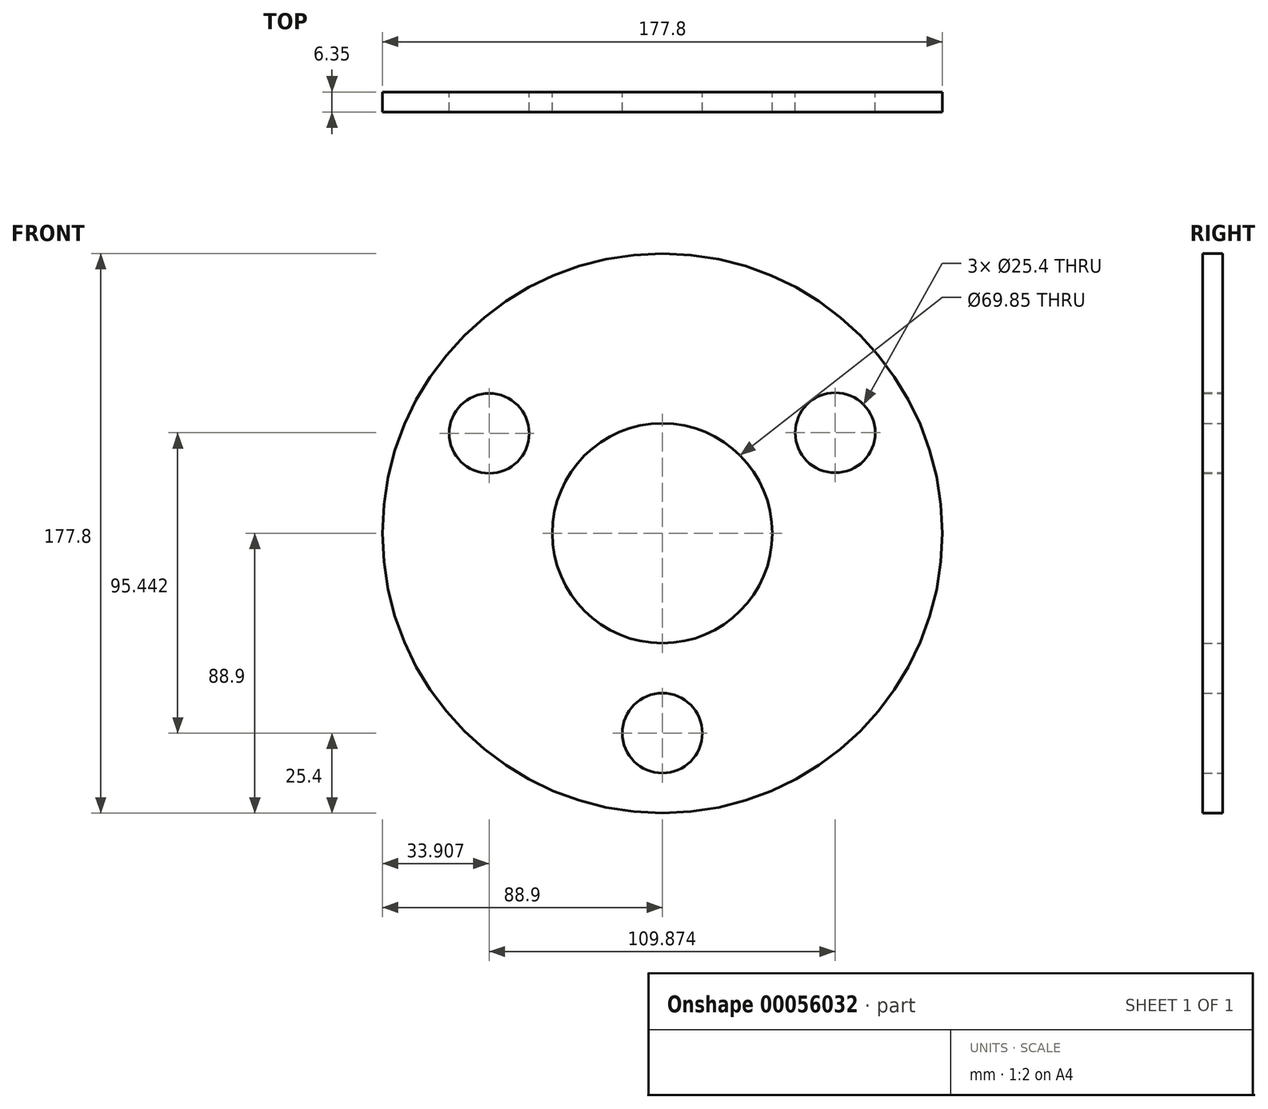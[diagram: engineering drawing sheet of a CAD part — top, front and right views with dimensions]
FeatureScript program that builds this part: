
annotation { "Feature Type Name" : "Feature", "Feature Type Description" : "" }
export const myFeature = defineFeature(function(context is Context, id is Id, definition is map)
    precondition{}
    {
        {
            var Q0;
            Q0=qCreatedBy(makeId("Front.planeOp"),FACE);
            var sketch = newSketch(context, id + "F0", { "sketchPlane" : qUnion([Q0])});
            skCircle(sketch, "E0", {"center": v(0, 0) * mm, "radius": 18.29 * mm});
            skCircle(sketch, "E1", {"center": v(0, 0) * mm, "radius": 34.93 * mm});
            skCircle(sketch, "E2", {"center": v(0, 0) * mm, "radius": 63.5 * mm, "construction": true});
            skCircle(sketch, "E3", {"center": v(0, 0) * mm, "radius": 88.9 * mm});
            skCircle(sketch, "E4", {"center": v(-55, 31.75) * mm, "radius": 12.7 * mm});
            skCircle(sketch, "E5", {"center": v(54.88, 31.94) * mm, "radius": 12.7 * mm});
            skCircle(sketch, "E6", {"center": v(0, -63.5) * mm, "radius": 12.7 * mm});
            skLineSegment(sketch, "E7", {"start": v(0, 0) * mm, "end": v(-88.55, 51.12) * mm});
            skLineSegment(sketch, "E8", {"start": v(0, 0) * mm, "end": v(89.93, 51.92) * mm});
            skSolve(sketch);
        }
        {
            var Q0;
            Q0 = qSketchRegion(id + "F0", true);
            extrude(context, id + "F1", {"entities" : qUnion([Q0]), "depth" : 6.35 * mm});
        }
    });
